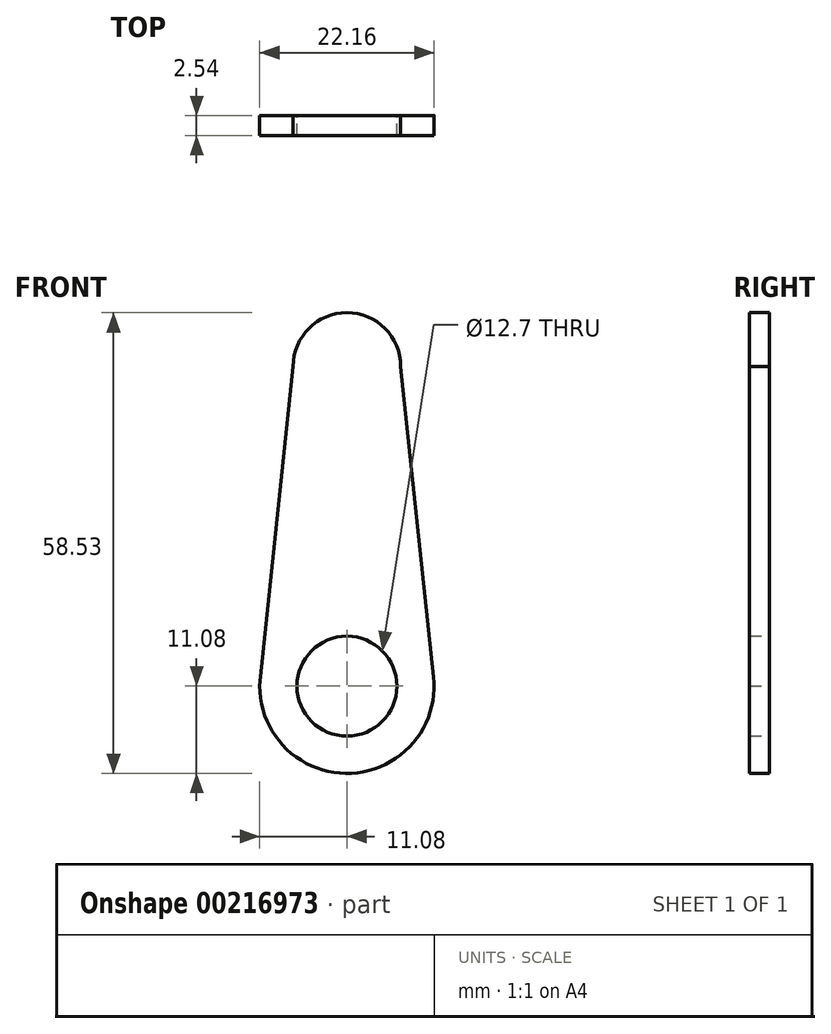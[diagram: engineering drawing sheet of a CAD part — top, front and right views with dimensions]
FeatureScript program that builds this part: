
annotation { "Feature Type Name" : "Feature", "Feature Type Description" : "" }
export const myFeature = defineFeature(function(context is Context, id is Id, definition is map)
    precondition{}
    {
        {
            var Q0;
            Q0=qCreatedBy(makeId("Front.planeOp"),FACE);
            var sketch = newSketch(context, id + "F0", { "sketchPlane" : qUnion([Q0])});
            skCircle(sketch, "E0", {"center": v(0, 0) * mm, "radius": 6.35 * mm});
            skArc(sketch, "E1", {"start": v(-10.84, 2.3) * mm, "mid": v(-0.57, -11.07) * mm, "end": v(11.02, 1.17) * mm});
            skArc(sketch, "E2", {"start": v(6.83, 40.62) * mm, "mid": v(0, 47.45) * mm, "end": v(-6.83, 40.62) * mm});
            skLineSegment(sketch, "E3", {"start": v(-11.08, 0) * mm, "end": v(-6.83, 40.62) * mm});
            skLineSegment(sketch, "E4", {"start": v(6.83, 40.62) * mm, "end": v(11.14, 0) * mm});
            skSolve(sketch);
        }
        {
            var Q0;
            Q0=makeQuery(id+"F0.imprint","IMPRINT",FACE,{"disambiguationData":[TD([[makeQuery(id+"F0.imprint","IMPRINT",EDGE,{"derivedFrom":sQuery(id+"F0.wireOp",EDGE,"E0")}),-1.0]])]});
            extrude(context, id + "F1", {"entities" : qUnion([Q0]), "depth" : 2.54 * mm});
        }
    });
